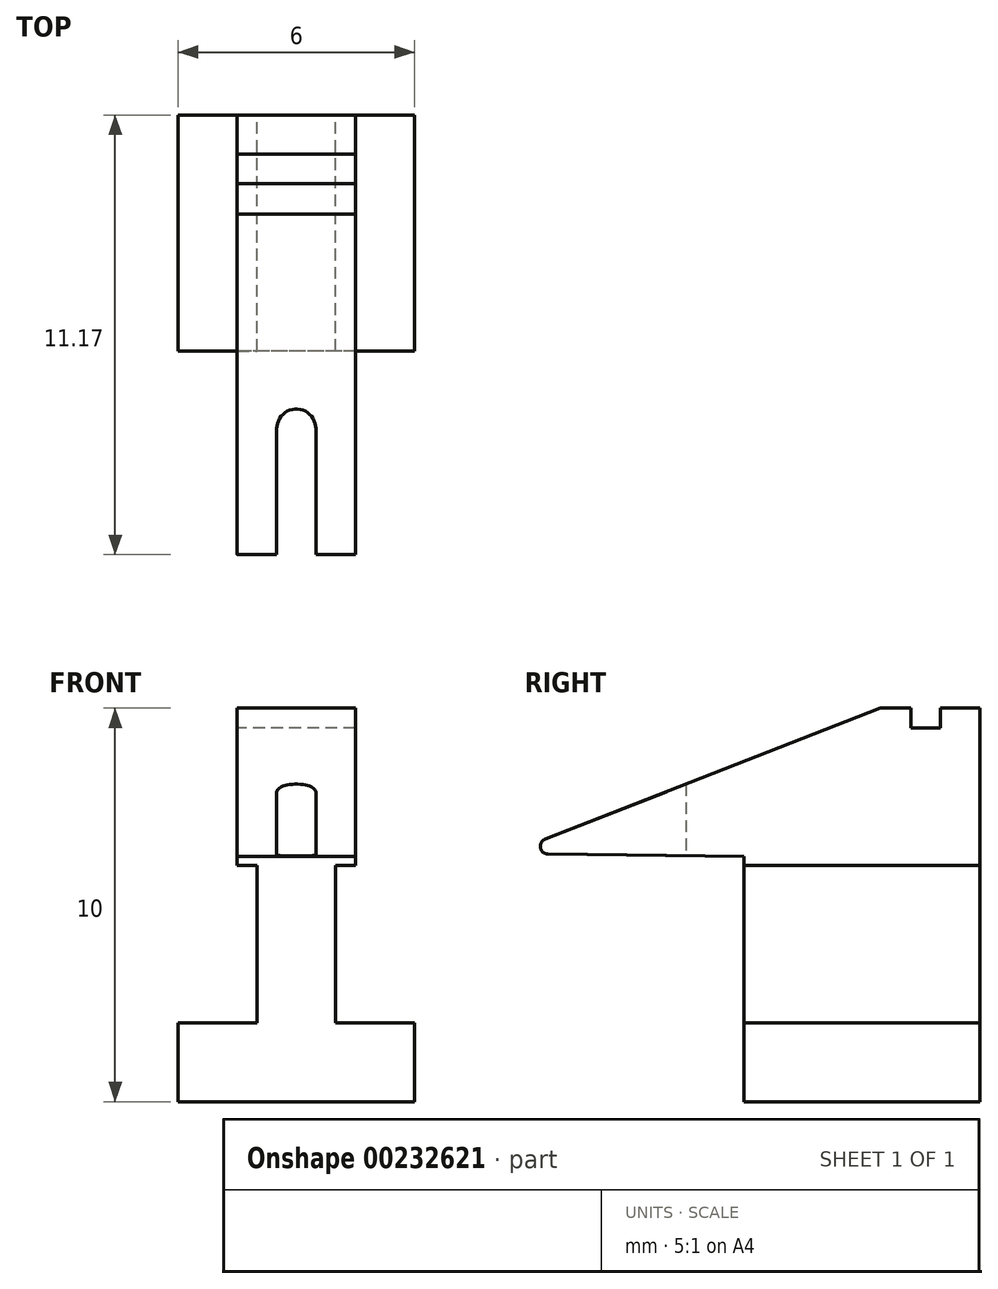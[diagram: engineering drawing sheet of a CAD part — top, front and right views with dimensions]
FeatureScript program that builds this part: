
annotation { "Feature Type Name" : "Feature", "Feature Type Description" : "" }
export const myFeature = defineFeature(function(context is Context, id is Id, definition is map)
    precondition{}
    {
        {
            var Q0;
            Q0=qCreatedBy(makeId("Front.planeOp"),FACE);
            var sketch = newSketch(context, id + "F0", { "sketchPlane" : qUnion([Q0])});
            skLineSegment(sketch, "E0", {"start": v(0, 0) * mm, "end": v(6, 0) * mm});
            skLineSegment(sketch, "E1", {"start": v(6, 0) * mm, "end": v(6, 2) * mm});
            skLineSegment(sketch, "E2", {"start": v(6, 2) * mm, "end": v(4, 2) * mm});
            skLineSegment(sketch, "E3", {"start": v(4, 2) * mm, "end": v(4, 6) * mm});
            skLineSegment(sketch, "E4", {"start": v(4, 6) * mm, "end": v(4.5, 6) * mm});
            skLineSegment(sketch, "E5", {"start": v(4.5, 6) * mm, "end": v(4.5, 10) * mm});
            skLineSegment(sketch, "E6", {"start": v(4.5, 10) * mm, "end": v(1.5, 10) * mm});
            skLineSegment(sketch, "E7", {"start": v(1.5, 10) * mm, "end": v(1.5, 6) * mm});
            skLineSegment(sketch, "E8", {"start": v(1.5, 6) * mm, "end": v(2, 6) * mm});
            skLineSegment(sketch, "E9", {"start": v(2, 6) * mm, "end": v(2, 2) * mm});
            skLineSegment(sketch, "E10", {"start": v(2, 2) * mm, "end": v(0, 2) * mm});
            skLineSegment(sketch, "E11", {"start": v(0, 2) * mm, "end": v(0, 0) * mm});
            skSolve(sketch);
        }
        {
            var Q0;
            Q0 = qSketchRegion(id + "F0", true);
            extrude(context, id + "F1", {"entities" : qUnion([Q0]), "depth" : 12 * mm});
        }
        {
            var Q0;
            Q0=makeQuery(id+"F1.opExtrude","SWEPT_FACE",FACE,{"disambiguationData":[OSD([sQuery(id+"F0.wireOp",EDGE,"E11")])]});
            var sketch = newSketch(context, id + "F2", { "sketchPlane" : qUnion([Q0])});
            skLineSegment(sketch, "E12", {"start": v(6, 0) * mm, "end": v(6, 6.23) * mm});
            skLineSegment(sketch, "E13", {"start": v(6, 6.23) * mm, "end": v(10.97, 6.29) * mm});
            skLineSegment(sketch, "E14", {"start": v(11.04, 6.67) * mm, "end": v(2.53, 10) * mm});
            skLineSegment(sketch, "E15", {"start": v(1, 10) * mm, "end": v(0, 10) * mm});
            skLineSegment(sketch, "E16", {"start": v(0, 10) * mm, "end": v(0, 10.68) * mm});
            skLineSegment(sketch, "E17", {"start": v(0, 10.68) * mm, "end": v(13.77, 10.68) * mm});
            skLineSegment(sketch, "E18", {"start": v(13.77, 10.68) * mm, "end": v(13.77, 0) * mm});
            skLineSegment(sketch, "E19", {"start": v(13.77, 0) * mm, "end": v(6, 0) * mm});
            skPoint(sketch, "E20.visualSharp", {"position": v(12, 6.3) * mm});
            skArc(sketch, "E20.filletArc", {"start": v(10.97, 6.29) * mm, "mid": v(11.17, 6.45) * mm, "end": v(11.04, 6.67) * mm});
            skLineSegment(sketch, "E21", {"start": v(2.53, 10) * mm, "end": v(1.75, 10) * mm});
            skLineSegment(sketch, "E22", {"start": v(1.75, 10) * mm, "end": v(1.75, 9.5) * mm});
            skLineSegment(sketch, "E23", {"start": v(1.75, 9.5) * mm, "end": v(1, 9.5) * mm});
            skLineSegment(sketch, "E24", {"start": v(1, 9.5) * mm, "end": v(1, 10) * mm});
            skSolve(sketch);
        }
        {
            var Q0;
            Q0 = qSketchRegion(id + "F2", true);
            extrude(context, id + "F3", {"entities" : qUnion([Q0]), "operationType" : NewBodyOperationType.REMOVE, "oppositeDirection" : true, "depth" : 25 * mm});
        }
        {
            var Q0;
            Q0=makeQuery(id+"F1.opExtrude","SWEPT_FACE",FACE,{"disambiguationData":[OSD([sQuery(id+"F0.wireOp",EDGE,"E0")])]});
            var sketch = newSketch(context, id + "F4", { "sketchPlane" : qUnion([Q0])});
            skLineSegment(sketch, "E25", {"start": v(3, 11.89) * mm, "end": v(3, 7.97) * mm});
            skArc(sketch, "E26.0.startCap", {"start": v(2.5, 11.89) * mm, "mid": v(3, 12.39) * mm, "end": v(3.5, 11.89) * mm});
            skArc(sketch, "E26.0.endCap", {"start": v(3.5, 7.97) * mm, "mid": v(3, 7.47) * mm, "end": v(2.5, 7.97) * mm});
            skLineSegment(sketch, "E26.0.left", {"start": v(3.5, 11.89) * mm, "end": v(3.5, 7.97) * mm});
            skLineSegment(sketch, "E26.0.right", {"start": v(2.5, 11.89) * mm, "end": v(2.5, 7.97) * mm});
            skSolve(sketch);
        }
        {
            var Q0;
            Q0 = qSketchRegion(id + "F4", true);
            extrude(context, id + "F5", {"entities" : qUnion([Q0]), "operationType" : NewBodyOperationType.REMOVE, "oppositeDirection" : true, "depth" : 25 * mm});
        }
    });
